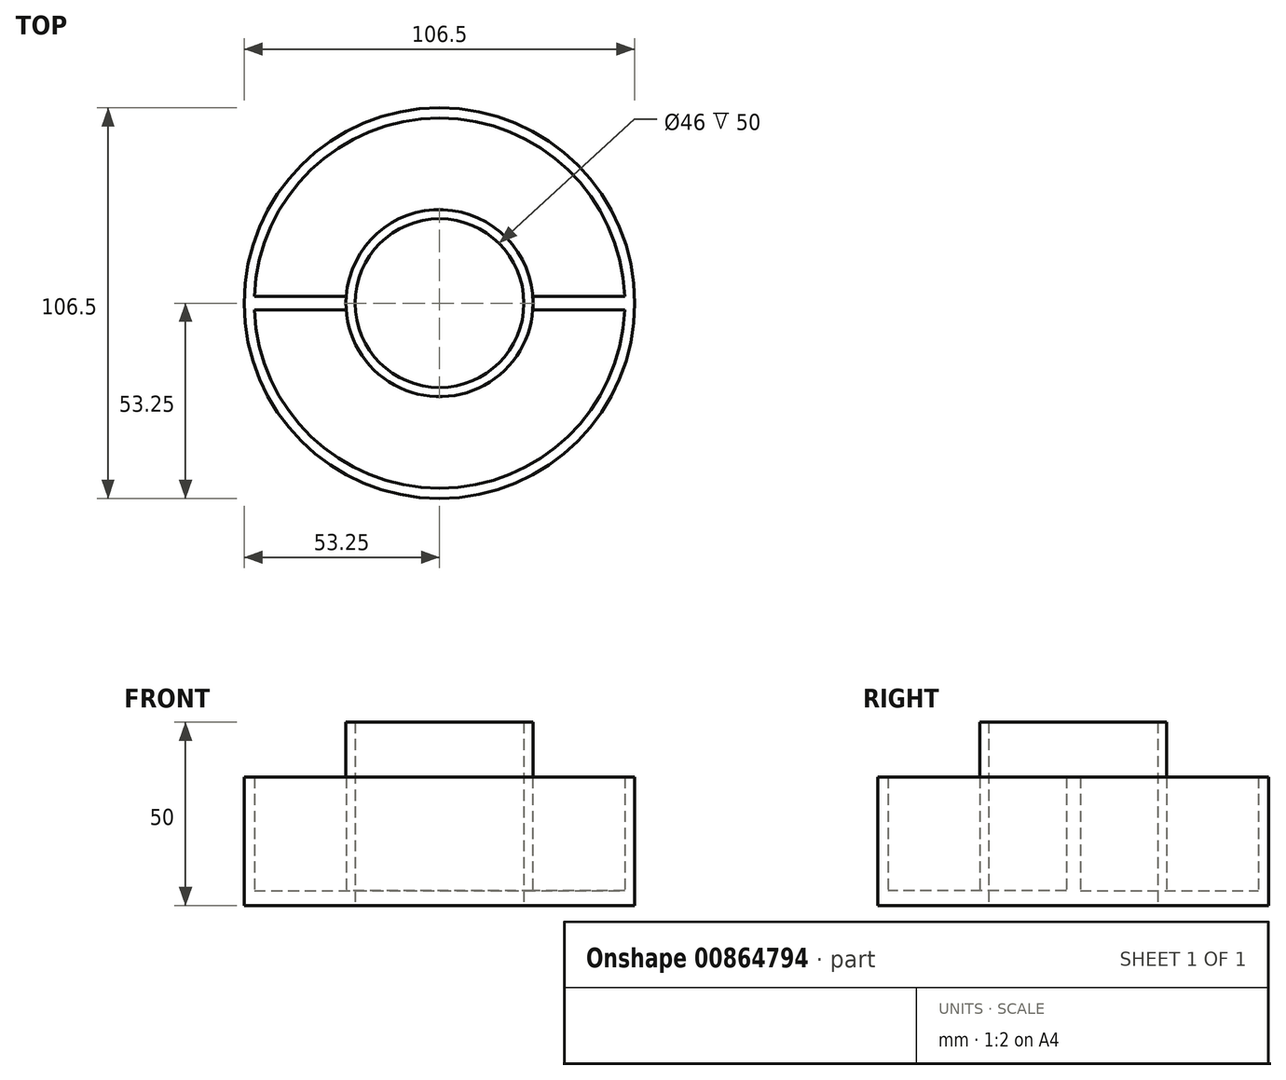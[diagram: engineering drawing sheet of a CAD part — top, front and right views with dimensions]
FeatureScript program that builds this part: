
annotation { "Feature Type Name" : "Feature", "Feature Type Description" : "" }
export const myFeature = defineFeature(function(context is Context, id is Id, definition is map)
    precondition{}
    {
        {
            var Q0;
            Q0=qCreatedBy(makeId("Top.planeOp"),FACE);
            var sketch = newSketch(context, id + "F0", { "sketchPlane" : qUnion([Q0])});
            skCircle(sketch, "E0", {"center": v(0, 0) * mm, "radius": 23 * mm});
            skCircle(sketch, "E1", {"center": v(0, 0) * mm, "radius": 25.5 * mm});
            skCircle(sketch, "E2", {"center": v(0, 0) * mm, "radius": 53.25 * mm});
            skCircle(sketch, "E3", {"center": v(0, 0) * mm, "radius": 50.5 * mm});
            skLineSegment(sketch, "E4", {"start": v(-50.46, 1.9) * mm, "end": v(-22.92, 1.9) * mm});
            skLineSegment(sketch, "E5.MirrorCS", {"start": v(-50.46, -1.9) * mm, "end": v(-22.92, -1.9) * mm});
            skLineSegment(sketch, "E6.MirrorCS", {"start": v(50.46, 1.9) * mm, "end": v(22.92, 1.9) * mm});
            skLineSegment(sketch, "E7.MirrorCS", {"start": v(50.46, -1.9) * mm, "end": v(22.92, -1.9) * mm});
            skSolve(sketch);
        }
        {
            var Q0;
            Q0=makeQuery(id+"F0.imprint","IMPRINT",FACE,{"disambiguationData":[TD([[makeQuery(id+"F0.imprint","IMPRINT",EDGE,{"derivedFrom":sQuery(id+"F0.wireOp",EDGE,"E2")}),1.0]])]});
            var Q1;
            {var subQ0=sQuery(id+"F0.wireOp",EDGE,"E4");var subQ1=sQuery(id+"F0.wireOp",EDGE,"E1");var subQ2=makeQuery(id+"F0.imprint","INTERSECT",VERTEX,{"derivedFrom":[subQ1,subQ0]});Q1=makeQuery(id+"F0.imprint","IMPRINT",FACE,{"disambiguationData":[TD([[makeQuery(id+"F0.imprint","IMPRINT",EDGE,{"disambiguationData":[TD([[subQ2,-1.0]])],"derivedFrom":subQ1}),-1.0]])]});}
            var Q2;
            {var subQ0=sQuery(id+"F0.wireOp",EDGE,"E6.MirrorCS");var subQ1=sQuery(id+"F0.wireOp",EDGE,"E1");var subQ2=makeQuery(id+"F0.imprint","INTERSECT",VERTEX,{"derivedFrom":[subQ1,subQ0]});Q2=makeQuery(id+"F0.imprint","IMPRINT",FACE,{"disambiguationData":[TD([[makeQuery(id+"F0.imprint","IMPRINT",EDGE,{"disambiguationData":[TD([[subQ2,1.0]])],"derivedFrom":subQ1}),-1.0]])]});}
            extrude(context, id + "F1", {"entities" : qUnion([Q0, Q1, Q2]), "depth" : 35 * mm, "offsetDistance" : 25 * mm});
        }
        {
            var Q0;
            {var subQ0=sQuery(id+"F0.wireOp",EDGE,"E4");var subQ1=sQuery(id+"F0.wireOp",EDGE,"E1");var subQ2=makeQuery(id+"F0.imprint","INTERSECT",VERTEX,{"derivedFrom":[subQ1,subQ0]});Q0=makeQuery(id+"F0.imprint","IMPRINT",FACE,{"disambiguationData":[TD([[makeQuery(id+"F0.imprint","IMPRINT",EDGE,{"disambiguationData":[TD([[subQ2,1.0]])],"derivedFrom":subQ1}),-1.0]])]});}
            var Q1;
            {var subQ0=sQuery(id+"F0.wireOp",EDGE,"E5.MirrorCS");var subQ1=sQuery(id+"F0.wireOp",EDGE,"E1");var subQ2=makeQuery(id+"F0.imprint","INTERSECT",VERTEX,{"derivedFrom":[subQ1,subQ0]});Q1=makeQuery(id+"F0.imprint","IMPRINT",FACE,{"disambiguationData":[TD([[makeQuery(id+"F0.imprint","IMPRINT",EDGE,{"disambiguationData":[TD([[subQ2,-1.0]])],"derivedFrom":subQ1}),-1.0]])]});}
            extrude(context, id + "F2", {"entities" : qUnion([Q0, Q1]), "operationType" : NewBodyOperationType.ADD, "depth" : 4 * mm, "offsetDistance" : 25 * mm});
        }
        {
            var Q0;
            {var subQ0=sQuery(id+"F0.wireOp",EDGE,"E4");var subQ1=sQuery(id+"F0.wireOp",EDGE,"E0");var subQ2=makeQuery(id+"F0.imprint","INTERSECT",VERTEX,{"derivedFrom":[subQ1,subQ0]});Q0=makeQuery(id+"F0.imprint","IMPRINT",FACE,{"disambiguationData":[TD([[makeQuery(id+"F0.imprint","IMPRINT",EDGE,{"disambiguationData":[TD([[subQ2,1.0]])],"derivedFrom":subQ1}),-1.0]])]});}
            var Q1;
            {var subQ0=sQuery(id+"F0.wireOp",EDGE,"E5.MirrorCS");var subQ1=sQuery(id+"F0.wireOp",EDGE,"E0");var subQ2=makeQuery(id+"F0.imprint","INTERSECT",VERTEX,{"derivedFrom":[subQ1,subQ0]});Q1=makeQuery(id+"F0.imprint","IMPRINT",FACE,{"disambiguationData":[TD([[makeQuery(id+"F0.imprint","IMPRINT",EDGE,{"disambiguationData":[TD([[subQ2,-1.0]])],"derivedFrom":subQ1}),-1.0]])]});}
            var Q2;
            {var subQ0=sQuery(id+"F0.wireOp",EDGE,"E4");var subQ1=sQuery(id+"F0.wireOp",EDGE,"E0");var subQ2=makeQuery(id+"F0.imprint","INTERSECT",VERTEX,{"derivedFrom":[subQ1,subQ0]});Q2=makeQuery(id+"F0.imprint","IMPRINT",FACE,{"disambiguationData":[TD([[makeQuery(id+"F0.imprint","IMPRINT",EDGE,{"disambiguationData":[TD([[subQ2,-1.0]])],"derivedFrom":subQ1}),-1.0]])]});}
            var Q3;
            {var subQ0=sQuery(id+"F0.wireOp",EDGE,"E6.MirrorCS");var subQ1=sQuery(id+"F0.wireOp",EDGE,"E0");var subQ2=makeQuery(id+"F0.imprint","INTERSECT",VERTEX,{"derivedFrom":[subQ1,subQ0]});Q3=makeQuery(id+"F0.imprint","IMPRINT",FACE,{"disambiguationData":[TD([[makeQuery(id+"F0.imprint","IMPRINT",EDGE,{"disambiguationData":[TD([[subQ2,1.0]])],"derivedFrom":subQ1}),-1.0]])]});}
            extrude(context, id + "F3", {"entities" : qUnion([Q0, Q1, Q2, Q3]), "operationType" : NewBodyOperationType.ADD, "depth" : 50 * mm, "offsetDistance" : 25 * mm});
        }
    });
